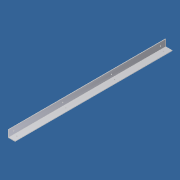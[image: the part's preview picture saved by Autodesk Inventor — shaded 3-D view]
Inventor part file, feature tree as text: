
AUTODESK INVENTOR PART (.ipt)
format: ipt  version: 2012 (Build 160160000, 160)  size: 90,624 bytes
history: native  units: in
note: dims shown in document units (in); Inventor stores cm internally (conversion verified against a paired STEP export)
features: hole x2, pattern_linear x2, extrude x1, sketch x1
ambient origin geometry x8: Origin, YZ Plane, XZ Plane, XY Plane, X Axis, Y Axis, Z Axis, Center Point
bodies: Solid1 (feature_tree)
feature tree (6):
  extrude  "Extrusion1"  Depth=0.125in
  hole  "Hole1"  [1 undecoded]
  pattern_linear  "Rectangular Pattern1"  Spacing1=2.0in  [1 undecoded]
  hole  "Hole2"  [1 undecoded]
  pattern_linear  "Rectangular Pattern2"  Count1=4 Spacing1=14.0in
  sketch  "Sketch1"  dims[d0=2.0in d1=0.125in d2=45.0in d3=0.0in d4=2.0in d5=1.0in d6=1.5in d7=0.265in d8=0.75in d9=0.375in d10=0.25in d11=0.5635in d12=1.0in d13=0.8108in d14=1.5748in d16=14.0in d17=1.5in d18=1.0in d19=0.265in d20=0.75in d21=0.375in d22=0.25in d23=0.5635in d24=1.0in d25=0.8108in d26=1.5748in d28=14.0in]
note: 3 required parameter values undecoded (feature->parameter linkage not recoverable at this tier; creation-order binding heuristic only, values carry confidence <= 0.55)
